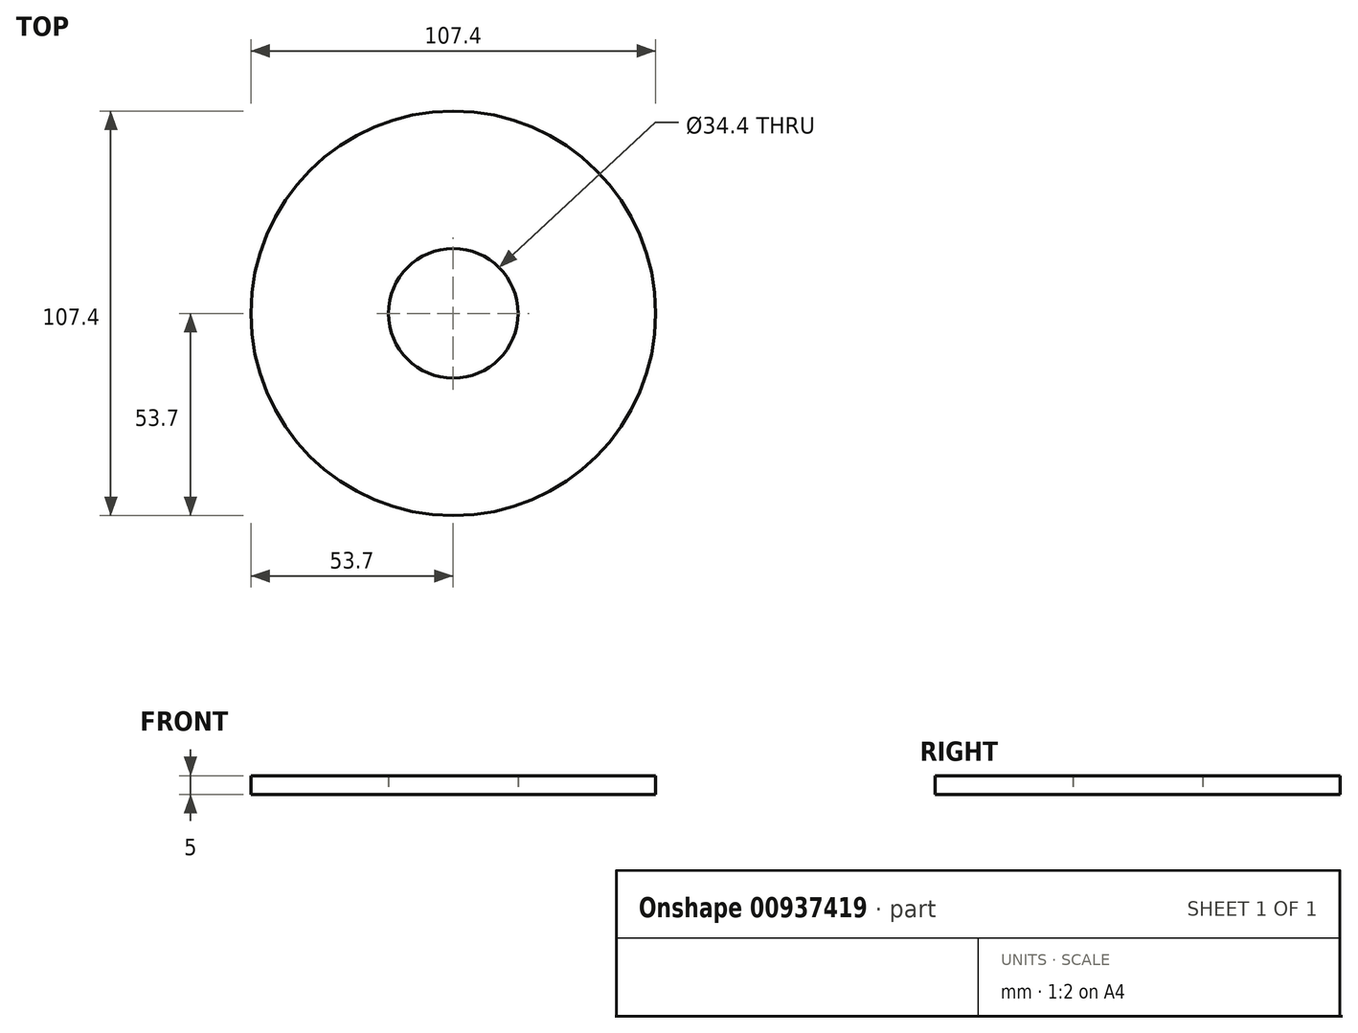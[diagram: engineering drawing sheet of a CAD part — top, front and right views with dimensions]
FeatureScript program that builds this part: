
annotation { "Feature Type Name" : "Feature", "Feature Type Description" : "" }
export const myFeature = defineFeature(function(context is Context, id is Id, definition is map)
    precondition{}
    {
        {
            var Q0;
            Q0=qCreatedBy(makeId("Top.planeOp"),FACE);
            var sketch = newSketch(context, id + "F0", { "sketchPlane" : qUnion([Q0])});
            skCircle(sketch, "E0", {"center": v(0, 0) * mm, "radius": 53.7 * mm});
            skSolve(sketch);
        }
        {
            var Q0;
            Q0=makeQuery(id+"F0.imprint","IMPRINT",FACE,{"disambiguationData":[TD([[makeQuery(id+"F0.imprint","IMPRINT",EDGE,{"derivedFrom":sQuery(id+"F0.wireOp",EDGE,"E0")}),1.0]])]});
            extrude(context, id + "F1", {"entities" : qUnion([Q0]), "depth" : 5 * mm, "offsetDistance" : 25 * mm});
        }
        {
            var Q0;
            Q0=makeQuery(id+"F1.opExtrude","CAP_FACE",FACE,{"disambiguationData":[OSD([sQuery(id+"F0.wireOp",EDGE,"E0")])],"isStart":true});
            var sketch = newSketch(context, id + "F2", { "sketchPlane" : qUnion([Q0])});
            skCircle(sketch, "E1", {"center": v(0, 0) * mm, "radius": 17.2 * mm});
            skSolve(sketch);
        }
        {
            var Q0;
            Q0=makeQuery(id+"F2.imprint","IMPRINT",FACE,{"disambiguationData":[TD([[makeQuery(id+"F2.imprint","IMPRINT",EDGE,{"derivedFrom":sQuery(id+"F2.wireOp",EDGE,"E1")}),1.0]])]});
            extrude(context, id + "F3", {"entities" : qUnion([Q0]), "operationType" : NewBodyOperationType.REMOVE, "endBound" : BoundingType.UP_TO_NEXT, "oppositeDirection" : true, "depth" : 25 * mm, "offsetDistance" : 25 * mm});
        }
    });
